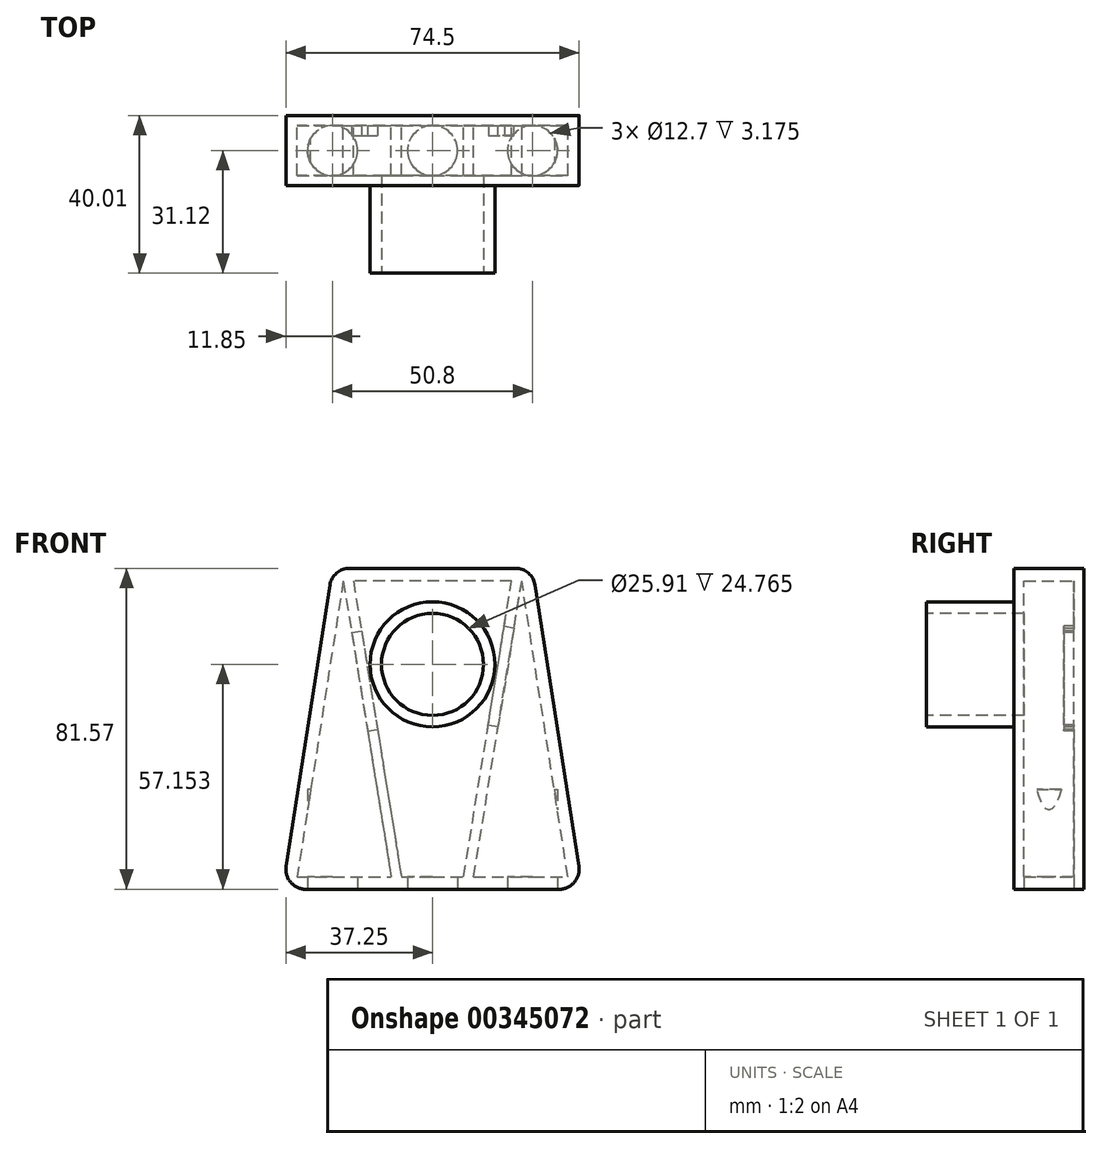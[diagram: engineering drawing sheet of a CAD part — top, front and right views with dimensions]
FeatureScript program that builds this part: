
annotation { "Feature Type Name" : "Feature", "Feature Type Description" : "" }
export const myFeature = defineFeature(function(context is Context, id is Id, definition is map)
    precondition{}
    {
        {
            var Q0;
            Q0=qCreatedBy(makeId("Front.planeOp"),FACE);
            var sketch = newSketch(context, id + "F0", { "sketchPlane" : qUnion([Q0])});
            skLineSegment(sketch, "E0", {"start": v(-25.4, 0) * mm, "end": v(-38.1, -81.57) * mm});
            skLineSegment(sketch, "E1", {"start": v(-38.1, -81.57) * mm, "end": v(38.1, -81.57) * mm});
            skLineSegment(sketch, "E2", {"start": v(38.1, -81.57) * mm, "end": v(25.4, 0) * mm});
            skLineSegment(sketch, "E3", {"start": v(25.4, 0) * mm, "end": v(-25.4, 0) * mm});
            skSolve(sketch);
        }
        {
            var Q0;
            Q0=makeQuery(id+"F0.imprint","IMPRINT",FACE,{"disambiguationData":[TD([[makeQuery(id+"F0.imprint","IMPRINT",EDGE,{"derivedFrom":sQuery(id+"F0.wireOp",EDGE,"E0")}),1.0]])]});
            extrude(context, id + "F1", {"entities" : qUnion([Q0]), "depth" : 2.54 * mm});
        }
        {
            var Q0;
            Q0=makeQuery(id+"F1.opExtrude","CAP_FACE",FACE,{"disambiguationData":[OSD([sQuery(id+"F0.wireOp",EDGE,"E0"),sQuery(id+"F0.wireOp",EDGE,"E1"),sQuery(id+"F0.wireOp",EDGE,"E2"),sQuery(id+"F0.wireOp",EDGE,"E3")])],"isStart":false});
            var sketch = newSketch(context, id + "F2", { "sketchPlane" : qUnion([Q0])});
            skLineSegment(sketch, "E4.0", {"start": v(22.68, -3.17) * mm, "end": v(-22.68, -3.18) * mm});
            skLineSegment(sketch, "E4.1", {"start": v(34.4, -78.4) * mm, "end": v(22.68, -3.17) * mm});
            skLineSegment(sketch, "E4.2", {"start": v(-34.4, -78.4) * mm, "end": v(34.4, -78.4) * mm});
            skLineSegment(sketch, "E4.3", {"start": v(-22.68, -3.17) * mm, "end": v(-34.4, -78.4) * mm});
            skLineSegment(sketch, "E5", {"start": v(-22.68, -3.17) * mm, "end": v(-10.48, -78.4) * mm});
            skLineSegment(sketch, "E6", {"start": v(10.48, -78.4) * mm, "end": v(22.68, -3.17) * mm});
            skLineSegment(sketch, "E7", {"start": v(-20.1, -3.17) * mm, "end": v(-7.9, -78.4) * mm});
            skLineSegment(sketch, "E8", {"start": v(7.9, -78.4) * mm, "end": v(20.1, -3.17) * mm});
            skSolve(sketch);
        }
        {
            var Q0;
            Q0=makeQuery(id+"F2.imprint","IMPRINT",FACE,{"disambiguationData":[TD([[makeQuery(id+"F2.imprint","IMPRINT",EDGE,{"derivedFrom":sQuery(id+"F2.wireOp",EDGE,"E4.0")}),-1.0]])]});
            var Q1;
            {var subQ0=sQuery(id+"F2.wireOp",EDGE,"E5");Q1=makeQuery(id+"F2.imprint","IMPRINT",FACE,{"disambiguationData":[TD([[makeQuery(id+"F2.imprint","IMPRINT",EDGE,{"derivedFrom":subQ0}),1.0]])]});}
            var Q2;
            {var subQ0=sQuery(id+"F2.wireOp",EDGE,"E6");Q2=makeQuery(id+"F2.imprint","IMPRINT",FACE,{"disambiguationData":[TD([[makeQuery(id+"F2.imprint","IMPRINT",EDGE,{"derivedFrom":subQ0}),1.0]])]});}
            extrude(context, id + "F3", {"entities" : qUnion([Q0, Q1, Q2]), "operationType" : NewBodyOperationType.ADD, "depth" : 6.35 * mm});
        }
        {
            var Q0;
            Q0=makeQuery(id+"F1.opExtrude","SWEPT_BODY",BODY,{"disambiguationData":[OSD([sQuery(id+"F0.wireOp",EDGE,"E0"),sQuery(id+"F0.wireOp",EDGE,"E1"),sQuery(id+"F0.wireOp",EDGE,"E2"),sQuery(id+"F0.wireOp",EDGE,"E3")])]});
            var Q1;
            Q1=makeQuery(id+"F3.opExtrude","CAP_FACE",FACE,{"disambiguationData":[OSD([sQuery(id+"F0.wireOp",EDGE,"E0"),sQuery(id+"F0.wireOp",EDGE,"E1"),sQuery(id+"F0.wireOp",EDGE,"E2"),sQuery(id+"F0.wireOp",EDGE,"E3"),sQuery(id+"F2.wireOp",EDGE,"E4.0"),sQuery(id+"F2.wireOp",EDGE,"E4.1"),sQuery(id+"F2.wireOp",EDGE,"E4.2"),sQuery(id+"F2.wireOp",EDGE,"E4.3")])],"isStart":false});
            mirror(context, id + "F4", {"operationType" : NewBodyOperationType.ADD, "entities" : qUnion([Q0]), "mirrorPlane" : qUnion([Q1])});
        }
        {
            var Q0;
            Q0=makeQuery(id+"F3.opExtrude","SWEPT_FACE",FACE,{"disambiguationData":[OSD([sQuery(id+"F2.wireOp",EDGE,"E6")])]});
            var sketch = newSketch(context, id + "F5", { "sketchPlane" : qUnion([Q0])});
            skLineSegment(sketch, "E9.bottom", {"start": v(-5.08, -11.6) * mm, "end": v(-2.54, -11.6) * mm});
            skLineSegment(sketch, "E9.top", {"start": v(-5.08, -37) * mm, "end": v(-2.54, -37) * mm});
            skLineSegment(sketch, "E9.left", {"start": v(-5.08, -11.6) * mm, "end": v(-5.08, -37) * mm});
            skLineSegment(sketch, "E9.right", {"start": v(-2.54, -11.6) * mm, "end": v(-2.54, -37) * mm});
            skPoint(sketch, "E9.middle", {"position": v(-3.8, -24.3) * mm});
            skSolve(sketch);
        }
        {
            var Q0;
            Q0=makeQuery(id+"F5.imprint","IMPRINT",FACE,{"disambiguationData":[TD([[makeQuery(id+"F5.imprint","IMPRINT",EDGE,{"derivedFrom":sQuery(id+"F5.wireOp",EDGE,"E9.bottom")}),-1.0]])]});
            extrude(context, id + "F6", {"entities" : qUnion([Q0]), "operationType" : NewBodyOperationType.REMOVE, "oppositeDirection" : true, "depth" : 6.35 * mm});
        }
        {
            var Q0;
            Q0=makeQuery(id+"F3.opExtrude","SWEPT_FACE",FACE,{"disambiguationData":[OSD([sQuery(id+"F2.wireOp",EDGE,"E7")])]});
            var sketch = newSketch(context, id + "F7", { "sketchPlane" : qUnion([Q0])});
            skLineSegment(sketch, "E10.bottom", {"start": v(-2.54, -12.8) * mm, "end": v(-5.08, -12.8) * mm});
            skLineSegment(sketch, "E10.top", {"start": v(-2.54, -38.2) * mm, "end": v(-5.08, -38.2) * mm});
            skLineSegment(sketch, "E10.left", {"start": v(-2.54, -12.8) * mm, "end": v(-2.54, -38.2) * mm});
            skLineSegment(sketch, "E10.right", {"start": v(-5.08, -12.8) * mm, "end": v(-5.08, -38.2) * mm});
            skPoint(sketch, "E10.middle", {"position": v(-3.8, -25.5) * mm});
            skSolve(sketch);
        }
        {
            var Q0;
            Q0 = qSketchRegion(id + "F7", true);
            extrude(context, id + "F8", {"entities" : qUnion([Q0]), "operationType" : NewBodyOperationType.REMOVE, "oppositeDirection" : true, "depth" : 6.35 * mm});
        }
        {
            var Q0;
            {var subQ0=sQuery(id+"F0.wireOp",EDGE,"E1");var subQ1=makeQuery(id+"F3.boolean.opBoolean","MERGE",FACE,{"derivedFrom":[makeQuery(id+"F1.opExtrude","SWEPT_FACE",FACE,{"disambiguationData":[OSD([subQ0])]}),makeQuery(id+"F3.opExtrude","SWEPT_FACE",FACE,{"disambiguationData":[OSD([subQ0])]})]});Q0=makeQuery(id+"F4.boolean.opBoolean","MERGE",FACE,{"derivedFrom":[subQ1,makeQuery(id+"F4.opPattern","COPY",FACE,{"derivedFrom":subQ1,"instanceName":"1"})]});}
            var sketch = newSketch(context, id + "F9", { "sketchPlane" : qUnion([Q0])});
            skCircle(sketch, "E11", {"center": v(-25.4, 8.9) * mm, "radius": 6.35 * mm});
            skCircle(sketch, "E12", {"center": v(0, 8.9) * mm, "radius": 6.35 * mm});
            skCircle(sketch, "E13", {"center": v(25.4, 8.9) * mm, "radius": 6.35 * mm});
            skSolve(sketch);
        }
        {
            var Q0;
            Q0=makeQuery(id+"F9.imprint","IMPRINT",FACE,{"disambiguationData":[TD([[makeQuery(id+"F9.imprint","IMPRINT",EDGE,{"derivedFrom":sQuery(id+"F9.wireOp",EDGE,"E11")}),1.0]])]});
            var Q1;
            Q1=makeQuery(id+"F9.imprint","IMPRINT",FACE,{"disambiguationData":[TD([[makeQuery(id+"F9.imprint","IMPRINT",EDGE,{"derivedFrom":sQuery(id+"F9.wireOp",EDGE,"E12")}),1.0]])]});
            var Q2;
            Q2=makeQuery(id+"F9.imprint","IMPRINT",FACE,{"disambiguationData":[TD([[makeQuery(id+"F9.imprint","IMPRINT",EDGE,{"derivedFrom":sQuery(id+"F9.wireOp",EDGE,"E13")}),1.0]])]});
            extrude(context, id + "F10", {"entities" : qUnion([Q0, Q1, Q2]), "operationType" : NewBodyOperationType.REMOVE, "oppositeDirection" : true, "depth" : 25.4 * mm});
        }
        {
            var Q0;
            Q0=makeQuery(id+"F4.opPattern","COPY",FACE,{"derivedFrom":makeQuery(id+"F1.opExtrude","CAP_FACE",FACE,{"disambiguationData":[OSD([sQuery(id+"F0.wireOp",EDGE,"E0"),sQuery(id+"F0.wireOp",EDGE,"E1"),sQuery(id+"F0.wireOp",EDGE,"E2"),sQuery(id+"F0.wireOp",EDGE,"E3")])],"isStart":true}),"instanceName":"1"});
            var sketch = newSketch(context, id + "F11", { "sketchPlane" : qUnion([Q0])});
            skCircle(sketch, "E14", {"center": v(0, -24.42) * mm, "radius": 15.88 * mm});
            skSolve(sketch);
        }
        {
            var Q0;
            Q0=makeQuery(id+"F11.imprint","IMPRINT",FACE,{"disambiguationData":[TD([[makeQuery(id+"F11.imprint","IMPRINT",EDGE,{"derivedFrom":sQuery(id+"F11.wireOp",EDGE,"E14")}),1.0]])]});
            extrude(context, id + "F12", {"entities" : qUnion([Q0]), "operationType" : NewBodyOperationType.ADD, "depth" : 22.22 * mm});
        }
        {
            var Q0;
            Q0=makeQuery(id+"F12.opExtrude","CAP_FACE",FACE,{"disambiguationData":[OSD([sQuery(id+"F11.wireOp",EDGE,"E14")])],"isStart":false});
            var sketch = newSketch(context, id + "F13", { "sketchPlane" : qUnion([Q0])});
            skCircle(sketch, "E15", {"center": v(0, -24.42) * mm, "radius": 12.95 * mm});
            skSolve(sketch);
        }
        {
            var Q0;
            Q0 = qSketchRegion(id + "F13", true);
            extrude(context, id + "F14", {"entities" : qUnion([Q0]), "operationType" : NewBodyOperationType.REMOVE, "oppositeDirection" : true, "depth" : 31.75 * mm});
        }
        {
            var Q0;
            Q0=makeQuery(id+"F12.opExtrude","CAP_EDGE",EDGE,{"disambiguationData":[OSD([sQuery(id+"F11.wireOp",EDGE,"E14")])],"isStart":true});
            var Q1;
            {var subQ0=sQuery(id+"F0.wireOp",EDGE,"E1");var subQ1=sQuery(id+"F0.wireOp",EDGE,"E0");var subQ2=makeQuery(id+"F3.boolean.opBoolean","MERGE",EDGE,{"derivedFrom":[makeQuery(id+"F1.opExtrude","SWEPT_EDGE",EDGE,{"disambiguationData":[OSD([subQ1,subQ0])]}),makeQuery(id+"F3.opExtrude","SWEPT_EDGE",EDGE,{"disambiguationData":[OSD([subQ1,subQ0])]})]});Q1=makeQuery(id+"F4.boolean.opBoolean","MERGE",EDGE,{"derivedFrom":[subQ2,makeQuery(id+"F4.opPattern","COPY",EDGE,{"derivedFrom":subQ2,"instanceName":"1"})]});}
            var Q2;
            {var subQ0=sQuery(id+"F0.wireOp",EDGE,"E2");var subQ1=sQuery(id+"F0.wireOp",EDGE,"E1");var subQ2=makeQuery(id+"F3.boolean.opBoolean","MERGE",EDGE,{"derivedFrom":[makeQuery(id+"F1.opExtrude","SWEPT_EDGE",EDGE,{"disambiguationData":[OSD([subQ1,subQ0])]}),makeQuery(id+"F3.opExtrude","SWEPT_EDGE",EDGE,{"disambiguationData":[OSD([subQ1,subQ0])]})]});Q2=makeQuery(id+"F4.boolean.opBoolean","MERGE",EDGE,{"derivedFrom":[subQ2,makeQuery(id+"F4.opPattern","COPY",EDGE,{"derivedFrom":subQ2,"instanceName":"1"})]});}
            var Q3;
            {var subQ0=sQuery(id+"F0.wireOp",EDGE,"E3");var subQ1=sQuery(id+"F0.wireOp",EDGE,"E2");var subQ2=makeQuery(id+"F3.boolean.opBoolean","MERGE",EDGE,{"derivedFrom":[makeQuery(id+"F1.opExtrude","SWEPT_EDGE",EDGE,{"disambiguationData":[OSD([subQ1,subQ0])]}),makeQuery(id+"F3.opExtrude","SWEPT_EDGE",EDGE,{"disambiguationData":[OSD([subQ1,subQ0])]})]});Q3=makeQuery(id+"F4.boolean.opBoolean","MERGE",EDGE,{"derivedFrom":[subQ2,makeQuery(id+"F4.opPattern","COPY",EDGE,{"derivedFrom":subQ2,"instanceName":"1"})]});}
            var Q4;
            {var subQ0=sQuery(id+"F0.wireOp",EDGE,"E3");var subQ1=sQuery(id+"F0.wireOp",EDGE,"E0");var subQ2=makeQuery(id+"F3.boolean.opBoolean","MERGE",EDGE,{"derivedFrom":[makeQuery(id+"F1.opExtrude","SWEPT_EDGE",EDGE,{"disambiguationData":[OSD([subQ1,subQ0])]}),makeQuery(id+"F3.opExtrude","SWEPT_EDGE",EDGE,{"disambiguationData":[OSD([subQ1,subQ0])]})]});Q4=makeQuery(id+"F4.boolean.opBoolean","MERGE",EDGE,{"derivedFrom":[subQ2,makeQuery(id+"F4.opPattern","COPY",EDGE,{"derivedFrom":subQ2,"instanceName":"1"})]});}
            fillet(context, id + "F15", {"entities" : qUnion([Q0, Q1, Q2, Q3, Q4]), "radius" : 5.08 * mm, "tangentPropagation" : true, "allowEdgeOverflow" : false});
        }
    });
